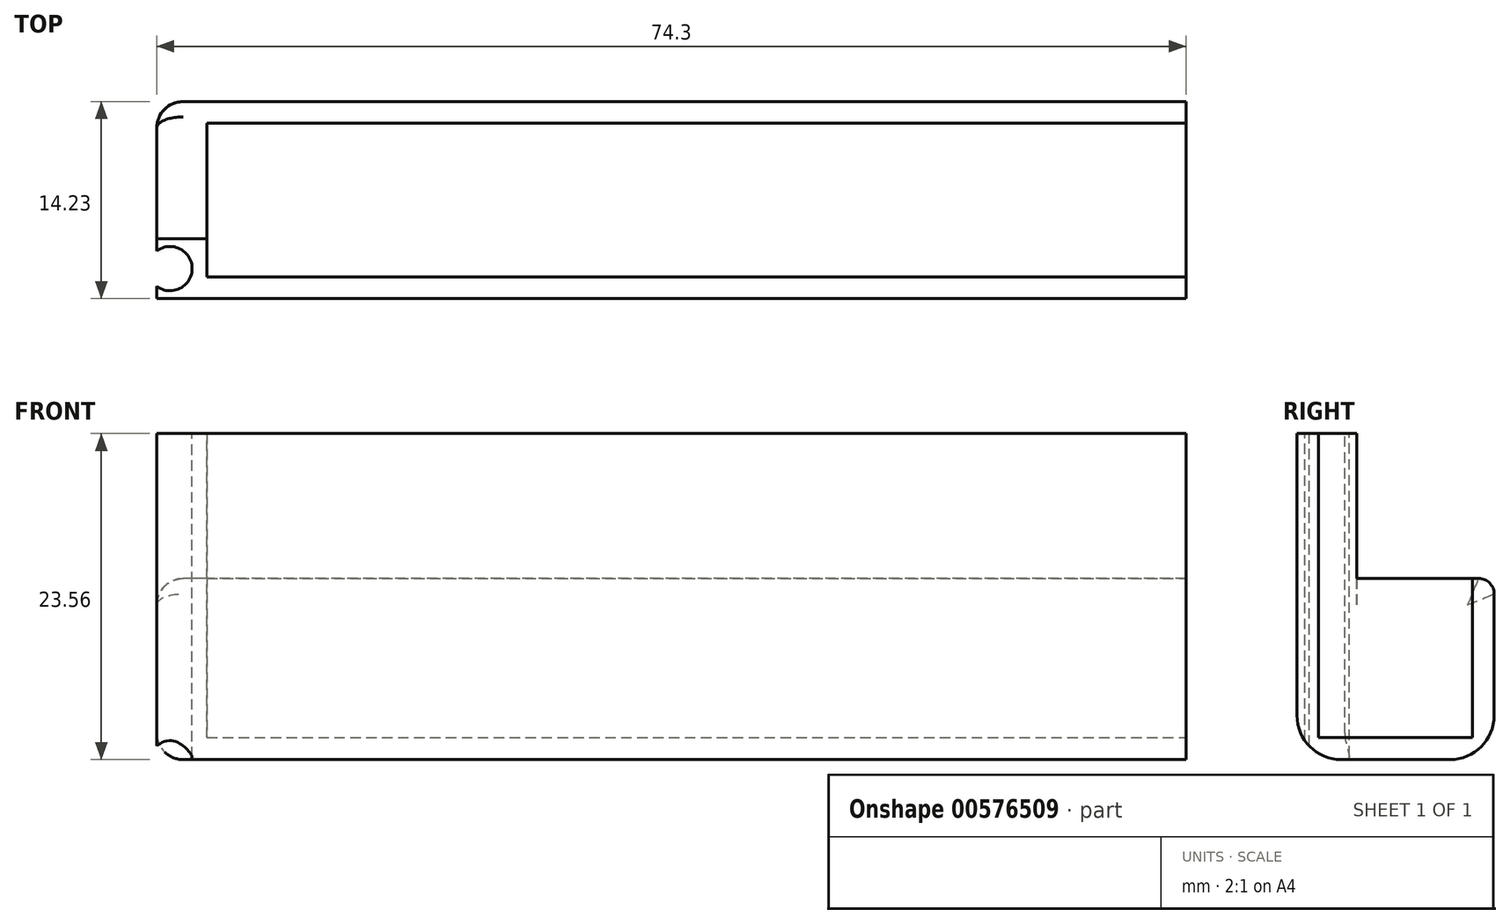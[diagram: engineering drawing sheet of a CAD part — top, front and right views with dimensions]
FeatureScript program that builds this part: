
annotation { "Feature Type Name" : "Feature", "Feature Type Description" : "" }
export const myFeature = defineFeature(function(context is Context, id is Id, definition is map)
    precondition{}
    {
        {
            var Q0;
            Q0=qCreatedBy(makeId("Front.planeOp"),FACE);
            var sketch = newSketch(context, id + "F0", { "sketchPlane" : qUnion([Q0])});
            skLineSegment(sketch, "E0.bottom", {"start": v(37.47, -12.06) * mm, "end": v(-37.46, -12.07) * mm});
            skLineSegment(sketch, "E0.top", {"start": v(37.46, 12.07) * mm, "end": v(-37.47, 12.06) * mm});
            skLineSegment(sketch, "E0.left", {"start": v(37.47, -12.06) * mm, "end": v(37.46, 12.07) * mm});
            skLineSegment(sketch, "E0.right", {"start": v(-37.46, -12.07) * mm, "end": v(-37.47, 12.06) * mm});
            skPoint(sketch, "E0.middle", {"position": v(0, 0) * mm});
            skSolve(sketch);
        }
        {
            var Q0;
            Q0=makeQuery(id+"F0.imprint","IMPRINT",FACE,{"disambiguationData":[TD([[makeQuery(id+"F0.imprint","IMPRINT",EDGE,{"derivedFrom":sQuery(id+"F0.wireOp",EDGE,"E0.bottom")}),-1.0]])]});
            extrude(context, id + "F1", {"entities" : qUnion([Q0]), "depth" : 4.32 * mm, "offsetDistance" : 25.4 * mm});
        }
        {
            var Q0;
            Q0=makeQuery(id+"F1.opExtrude","SWEPT_FACE",FACE,{"disambiguationData":[OSD([sQuery(id+"F0.wireOp",EDGE,"E0.top")])]});
            var sketch = newSketch(context, id + "F2", { "sketchPlane" : qUnion([Q0])});
            skLineSegment(sketch, "E1", {"start": v(-37.47, -2.16) * mm, "end": v(-35.88, -2.16) * mm});
            skCircle(sketch, "E2", {"center": v(-35.88, -2.16) * mm, "radius": 1.6 * mm});
            skPoint(sketch, "E3", {"position": v(-34.28, -2.16) * mm});
            skSolve(sketch);
        }
        {
            var Q0;
            {var subQ0=sQuery(id+"F2.wireOp",EDGE,"E2");var subQ1=makeQuery(id+"F1.opExtrude","SWEPT_EDGE",EDGE,{"disambiguationData":[OSD([sQuery(id+"F0.wireOp",EDGE,"E0.top"),sQuery(id+"F0.wireOp",EDGE,"E0.right")])]});var subQ2=makeQuery(id+"F2.imprint","INTERSECT",VERTEX,{"disambiguationData":[OD(0.0)],"derivedFrom":[subQ1,subQ0]});Q0=makeQuery(id+"F2.imprint","IMPRINT",FACE,{"disambiguationData":[TD([[makeQuery(id+"F2.imprint","IMPRINT",EDGE,{"disambiguationData":[TD([[subQ2,1.0]])],"derivedFrom":subQ0}),1.0]])]});}
            extrude(context, id + "F3", {"entities" : qUnion([Q0]), "operationType" : NewBodyOperationType.REMOVE, "oppositeDirection" : true, "depth" : 25.4 * mm, "offsetDistance" : 25.4 * mm});
        }
        {
            var Q0;
            {var subQ0=sQuery(id+"F0.wireOp",EDGE,"E0.bottom");var subQ1=sQuery(id+"F0.wireOp",EDGE,"E0.right");var subQ2=sQuery(id+"F0.wireOp",EDGE,"E0.top");Q0=makeQuery(id+"F3.boolean.opBoolean","SPLIT",FACE,{"disambiguationData":[TD([makeQuery(id+"F1.opExtrude","CAP_FACE",FACE,{"disambiguationData":[OSD([subQ0,subQ2,sQuery(id+"F0.wireOp",EDGE,"E0.left"),subQ1])],"isStart":false})])],"derivedFrom":makeQuery(id+"F1.opExtrude","SWEPT_FACE",FACE,{"disambiguationData":[OSD([subQ1])]})});}
            var Q1;
            {var subQ0=sQuery(id+"F0.wireOp",EDGE,"E0.bottom");var subQ1=sQuery(id+"F0.wireOp",EDGE,"E0.right");var subQ2=sQuery(id+"F0.wireOp",EDGE,"E0.top");Q1=makeQuery(id+"F3.boolean.opBoolean","SPLIT",FACE,{"disambiguationData":[TD([makeQuery(id+"F1.opExtrude","CAP_FACE",FACE,{"disambiguationData":[OSD([subQ0,subQ2,sQuery(id+"F0.wireOp",EDGE,"E0.left"),subQ1])],"isStart":true})])],"derivedFrom":makeQuery(id+"F1.opExtrude","SWEPT_FACE",FACE,{"disambiguationData":[OSD([subQ1])]})});}
            extrude(context, id + "F4", {"entities" : qUnion([Q0, Q1]), "operationType" : NewBodyOperationType.REMOVE, "oppositeDirection" : true, "depth" : 0.64 * mm, "offsetDistance" : 25.4 * mm});
        }
        {
            var Q0;
            Q0=makeQuery(id+"F1.opExtrude","CAP_FACE",FACE,{"disambiguationData":[OSD([sQuery(id+"F0.wireOp",EDGE,"E0.bottom"),sQuery(id+"F0.wireOp",EDGE,"E0.top"),sQuery(id+"F0.wireOp",EDGE,"E0.left"),sQuery(id+"F0.wireOp",EDGE,"E0.right")])],"isStart":true});
            var sketch = newSketch(context, id + "F5", { "sketchPlane" : qUnion([Q0])});
            skLineSegment(sketch, "E4.bottom", {"start": v(-37.46, -12.06) * mm, "end": v(36.83, -12.06) * mm});
            skLineSegment(sketch, "E4.top", {"start": v(-37.46, 0) * mm, "end": v(36.83, 0) * mm});
            skLineSegment(sketch, "E4.left", {"start": v(-37.47, -12.06) * mm, "end": v(-37.47, 0) * mm});
            skLineSegment(sketch, "E4.right", {"start": v(36.83, -12.07) * mm, "end": v(36.83, 0) * mm});
            skSolve(sketch);
        }
        {
            var Q0;
            Q0=makeQuery(id+"F5.imprint","IMPRINT",FACE,{"disambiguationData":[TD([[makeQuery(id+"F5.imprint","IMPRINT",EDGE,{"derivedFrom":sQuery(id+"F5.wireOp",EDGE,"E4.bottom")}),1.0]])]});
            extrude(context, id + "F6", {"entities" : qUnion([Q0]), "operationType" : NewBodyOperationType.ADD, "depth" : 8.9 * mm, "offsetDistance" : 25.4 * mm});
        }
        {
            var Q0;
            Q0=makeQuery(id+"F6.opExtrude","CAP_FACE",FACE,{"disambiguationData":[OSD([sQuery(id+"F5.wireOp",EDGE,"E4.bottom"),sQuery(id+"F5.wireOp",EDGE,"E4.top"),sQuery(id+"F5.wireOp",EDGE,"E4.left"),sQuery(id+"F5.wireOp",EDGE,"E4.right")])],"isStart":false});
            extrude(context, id + "F7", {"entities" : qUnion([Q0]), "operationType" : NewBodyOperationType.ADD, "depth" : 1.02 * mm, "offsetDistance" : 25.4 * mm});
        }
        {
            var Q0;
            {var subQ0=sQuery(id+"F5.wireOp",EDGE,"E4.bottom");Q0=makeQuery(id+"F7.boolean.opBoolean","MERGE",FACE,{"derivedFrom":[makeQuery(id+"F6.boolean.opBoolean","MERGE",FACE,{"derivedFrom":[makeQuery(id+"F1.opExtrude","SWEPT_FACE",FACE,{"disambiguationData":[OSD([sQuery(id+"F0.wireOp",EDGE,"E0.bottom")])]}),makeQuery(id+"F6.opExtrude","SWEPT_FACE",FACE,{"disambiguationData":[OSD([subQ0])]})]}),makeQuery(id+"F7.opExtrude","SWEPT_FACE",FACE,{"disambiguationData":[OSD([subQ0])]})]});}
            extrude(context, id + "F8", {"entities" : qUnion([Q0]), "operationType" : NewBodyOperationType.ADD, "depth" : 1.02 * mm, "offsetDistance" : 25.4 * mm});
        }
        {
            var Q0;
            {var subQ0=sQuery(id+"F5.wireOp",EDGE,"E4.left");var subQ1=sQuery(id+"F0.wireOp",EDGE,"E0.left");Q0=makeQuery(id+"F8.boolean.opBoolean","MERGE",FACE,{"derivedFrom":[makeQuery(id+"F7.boolean.opBoolean","MERGE",FACE,{"derivedFrom":[makeQuery(id+"F6.boolean.opBoolean","MERGE",FACE,{"derivedFrom":[makeQuery(id+"F1.opExtrude","SWEPT_FACE",FACE,{"disambiguationData":[OSD([subQ1])]}),makeQuery(id+"F6.opExtrude","SWEPT_FACE",FACE,{"disambiguationData":[OSD([subQ0])]})]}),makeQuery(id+"F7.opExtrude","SWEPT_FACE",FACE,{"disambiguationData":[OSD([subQ0])]})]}),makeQuery(id+"F8.opExtrude","SWEPT_FACE",FACE,{"disambiguationData":[OSD([sQuery(id+"F0.wireOp",EDGE,"E0.bottom"),subQ1,sQuery(id+"F5.wireOp",EDGE,"E4.bottom"),subQ0])]})]});}
            var sketch = newSketch(context, id + "F9", { "sketchPlane" : qUnion([Q0])});
            skLineSegment(sketch, "E5", {"start": v(0, 12.06) * mm, "end": v(0, 10.48) * mm});
            skLineSegment(sketch, "E6", {"start": v(-4.32, 12.06) * mm, "end": v(-2.77, 12.06) * mm});
            skLineSegment(sketch, "E7", {"start": v(9.9, 0) * mm, "end": v(8.36, 0) * mm});
            skLineSegment(sketch, "E8", {"start": v(-4.32, -13.08) * mm, "end": v(-4.32, -11.5) * mm});
            skLineSegment(sketch, "E9", {"start": v(-2.77, 12.06) * mm, "end": v(-2.77, -11.5) * mm});
            skLineSegment(sketch, "E10", {"start": v(-2.77, -11.5) * mm, "end": v(8.36, -11.5) * mm});
            skLineSegment(sketch, "E11", {"start": v(8.36, -11.5) * mm, "end": v(8.36, 0) * mm});
            skSolve(sketch);
        }
        {
            var Q0;
            {var subQ2=sQuery(id+"F9.wireOp",EDGE,"E5");Q0=makeQuery(id+"F9.imprint","IMPRINT",FACE,{"disambiguationData":[TD([[makeQuery(id+"F9.imprint","IMPRINT",EDGE,{"derivedFrom":subQ2}),1.0]])]});}
            extrude(context, id + "F10", {"entities" : qUnion([Q0]), "operationType" : NewBodyOperationType.REMOVE, "oppositeDirection" : true, "depth" : 68.58 * mm, "offsetDistance" : 25.4 * mm, "hasSecondDirection" : true, "secondDirectionOppositeDirection" : true, "secondDirectionDepth" : 1.59 * mm});
        }
        {
            var Q0;
            Q0=makeQuery(id+"F10.boolean.opBoolean","COPY",FACE,{"derivedFrom":makeQuery(id+"F10.opExtrude","CAP_FACE",FACE,{"disambiguationData":[OSD([sQuery(id+"F0.wireOp",EDGE,"E0.top"),sQuery(id+"F0.wireOp",EDGE,"E0.left"),sQuery(id+"F5.wireOp",EDGE,"E4.top"),sQuery(id+"F5.wireOp",EDGE,"E4.left"),sQuery(id+"F9.wireOp",EDGE,"E5"),sQuery(id+"F9.wireOp",EDGE,"E9"),sQuery(id+"F9.wireOp",EDGE,"E10"),sQuery(id+"F9.wireOp",EDGE,"E11")])],"isStart":true})});
            extrude(context, id + "F11", {"entities" : qUnion([Q0]), "operationType" : NewBodyOperationType.REMOVE, "oppositeDirection" : true, "depth" : 25.4 * mm, "offsetDistance" : 25.4 * mm});
        }
        {
            var Q0;
            Q0=makeQuery(id+"F8.opExtrude","CAP_EDGE",EDGE,{"disambiguationData":[OSD([sQuery(id+"F5.wireOp",EDGE,"E4.bottom")])],"isStart":false});
            fillet(context, id + "F12", {"entities" : qUnion([Q0]), "radius" : 3.17 * mm, "tangentPropagation" : true, "allowEdgeOverflow" : false});
        }
        {
            var Q0;
            Q0=makeQuery(id+"F8.opExtrude","CAP_EDGE",EDGE,{"disambiguationData":[OSD([sQuery(id+"F0.wireOp",EDGE,"E0.bottom")])],"isStart":false});
            fillet(context, id + "F13", {"entities" : qUnion([Q0]), "radius" : 3.17 * mm, "tangentPropagation" : true, "allowEdgeOverflow" : false});
        }
        {
            var Q0;
            Q0=makeQuery(id+"F7.opExtrude","CAP_EDGE",EDGE,{"disambiguationData":[OSD([sQuery(id+"F5.wireOp",EDGE,"E4.top")])],"isStart":false});
            fillet(context, id + "F14", {"entities" : qUnion([Q0]), "radius" : 1.1 * mm, "tangentPropagation" : true, "allowEdgeOverflow" : false});
        }
        {
            var Q0;
            {var subQ0=sQuery(id+"F5.wireOp",EDGE,"E4.right");Q0=makeQuery(id+"F8.boolean.opBoolean","MERGE",EDGE,{"derivedFrom":[makeQuery(id+"F7.opExtrude","CAP_EDGE",EDGE,{"disambiguationData":[OSD([subQ0])],"isStart":false}),makeQuery(id+"F8.opExtrude","SWEPT_EDGE",EDGE,{"disambiguationData":[OSD([sQuery(id+"F5.wireOp",EDGE,"E4.bottom"),subQ0])]})]});}
            fillet(context, id + "F15", {"entities" : qUnion([Q0]), "radius" : 1.9 * mm, "tangentPropagation" : true, "allowEdgeOverflow" : false});
        }
        {
            var Q0;
            Q0=makeQuery(id+"F10.boolean.opBoolean","COPY",FACE,{"derivedFrom":makeQuery(id+"F10.opExtrude","CAP_FACE",FACE,{"disambiguationData":[OSD([sQuery(id+"F0.wireOp",EDGE,"E0.top"),sQuery(id+"F0.wireOp",EDGE,"E0.left"),sQuery(id+"F5.wireOp",EDGE,"E4.top"),sQuery(id+"F5.wireOp",EDGE,"E4.left"),sQuery(id+"F9.wireOp",EDGE,"E5"),sQuery(id+"F9.wireOp",EDGE,"E9"),sQuery(id+"F9.wireOp",EDGE,"E10"),sQuery(id+"F9.wireOp",EDGE,"E11")])],"isStart":false})});
            extrude(context, id + "F16", {"entities" : qUnion([Q0]), "operationType" : NewBodyOperationType.REMOVE, "oppositeDirection" : true, "depth" : 2.1 * mm, "offsetDistance" : 25.4 * mm});
        }
        {
            var Q0;
            Q0=makeQuery(id+"F1.opExtrude","SWEPT_FACE",FACE,{"disambiguationData":[OSD([sQuery(id+"F0.wireOp",EDGE,"E0.top")])]});
            extrude(context, id + "F17", {"entities" : qUnion([Q0]), "operationType" : NewBodyOperationType.REMOVE, "oppositeDirection" : true, "depth" : 1.59 * mm, "offsetDistance" : 25.4 * mm});
        }
    });
